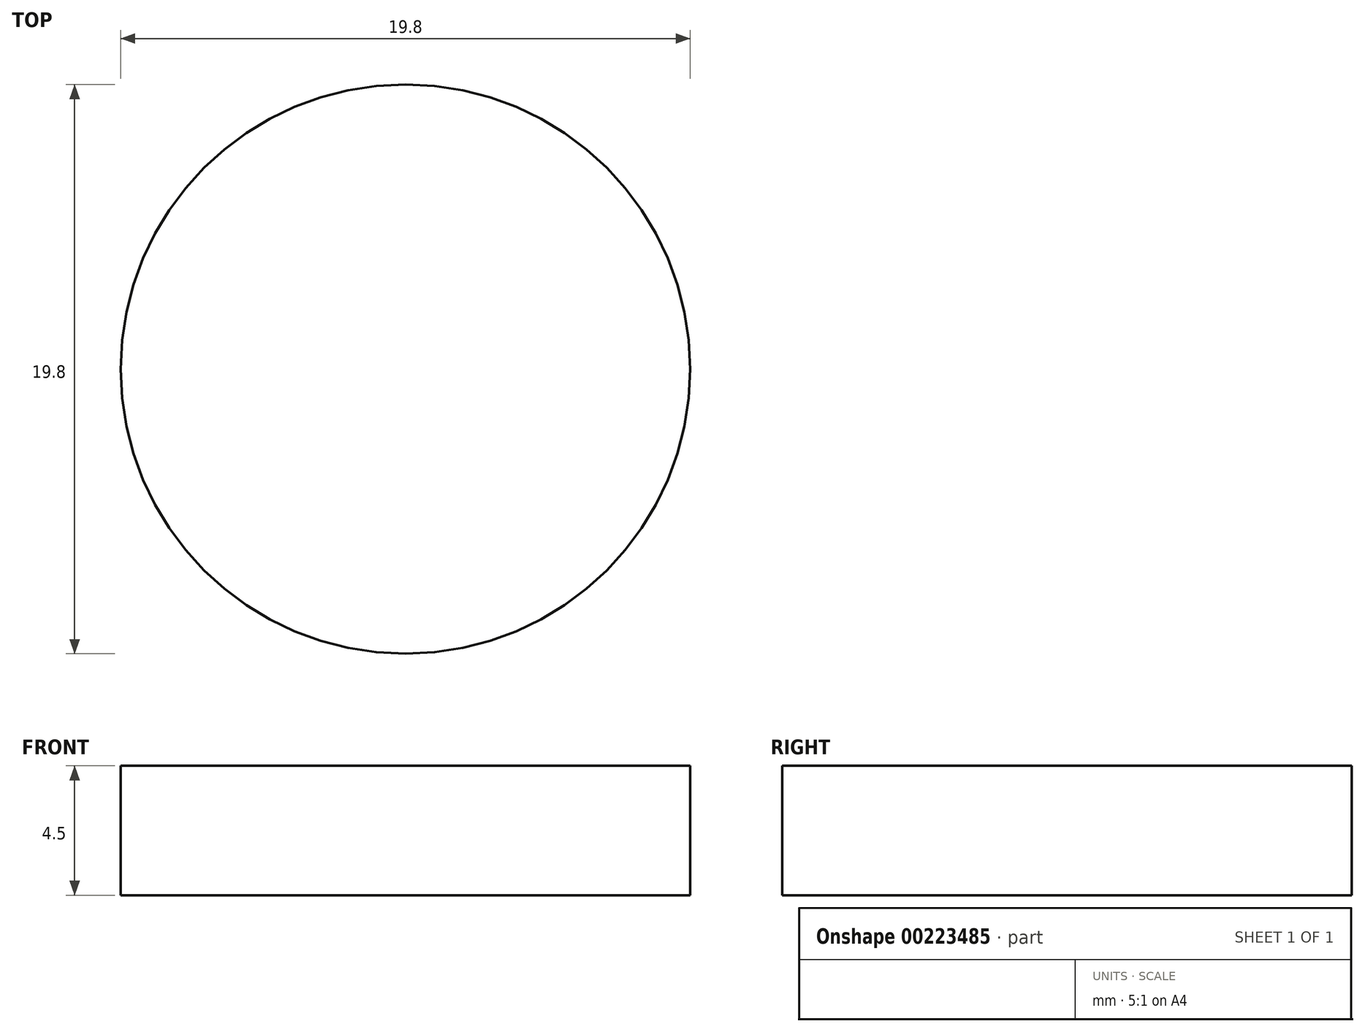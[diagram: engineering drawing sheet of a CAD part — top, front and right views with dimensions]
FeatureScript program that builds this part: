
annotation { "Feature Type Name" : "Feature", "Feature Type Description" : "" }
export const myFeature = defineFeature(function(context is Context, id is Id, definition is map)
    precondition{}
    {
        {
            assignVariable(context, id + "F0", {"name" : "PlungerHeight", "anyValue" : 6 - 1.5});
        }
        {
            var Q0;
            Q0=qCreatedBy(makeId("Top.planeOp"),FACE);
            var sketch = newSketch(context, id + "F1", { "sketchPlane" : qUnion([Q0])});
            skCircle(sketch, "E0", {"center": v(0, 0) * mm, "radius": 9.9 * mm});
            skSolve(sketch);
        }
        {
            var Q0;
            Q0 = qSketchRegion(id + "F1", true);
            extrude(context, id + "F2", {"entities" : qUnion([Q0]), "depth" : (getVariable(context, 'PlungerHeight')) * mm});
        }
    });
